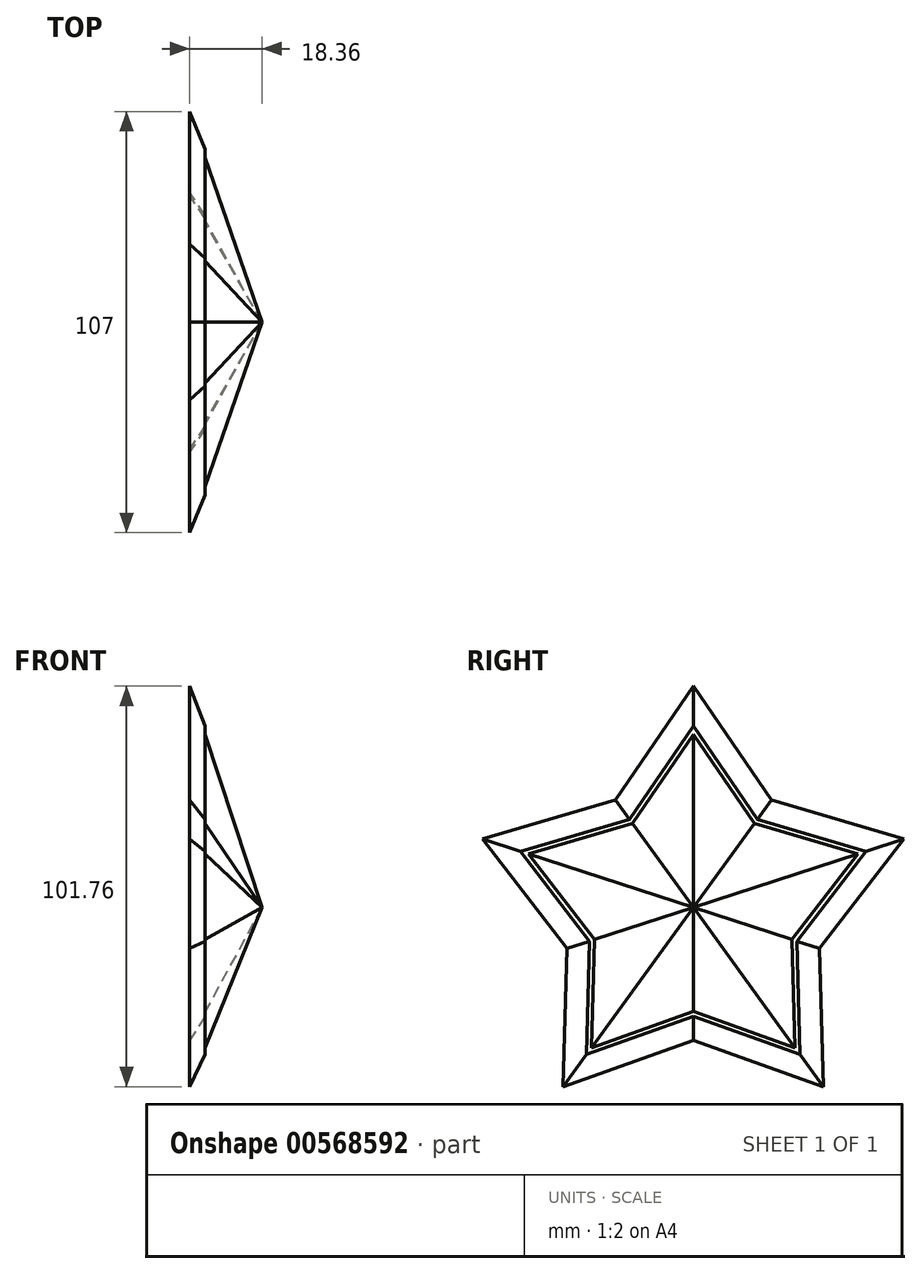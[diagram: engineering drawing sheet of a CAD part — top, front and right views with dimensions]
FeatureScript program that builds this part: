
annotation { "Feature Type Name" : "Feature", "Feature Type Description" : "" }
export const myFeature = defineFeature(function(context is Context, id is Id, definition is map)
    precondition{}
    {
        {
            var Q0;
            Q0=qCreatedBy(makeId("Right.planeOp"),FACE);
            var sketch = newSketch(context, id + "F0", { "sketchPlane" : qUnion([Q0])});
            skLineSegment(sketch, "E0", {"start": v(-53.5, 17.38) * mm, "end": v(-32.1, -10.43) * mm});
            skLineSegment(sketch, "E1", {"start": v(-32.1, -10.43) * mm, "end": v(-33.06, -45.5) * mm});
            skLineSegment(sketch, "E2", {"start": v(-33.06, -45.5) * mm, "end": v(0, -33.75) * mm});
            skLineSegment(sketch, "E3", {"start": v(0, -33.75) * mm, "end": v(33.06, -45.5) * mm});
            skLineSegment(sketch, "E4", {"start": v(33.06, -45.5) * mm, "end": v(32.1, -10.43) * mm});
            skLineSegment(sketch, "E5", {"start": v(32.1, -10.43) * mm, "end": v(53.5, 17.38) * mm});
            skLineSegment(sketch, "E6", {"start": v(53.5, 17.38) * mm, "end": v(19.84, 27.3) * mm});
            skLineSegment(sketch, "E7", {"start": v(19.84, 27.3) * mm, "end": v(0, 56.25) * mm});
            skLineSegment(sketch, "E8", {"start": v(0, 56.25) * mm, "end": v(-19.84, 27.3) * mm});
            skLineSegment(sketch, "E9", {"start": v(-19.84, 27.3) * mm, "end": v(-53.5, 17.38) * mm});
            skLineSegment(sketch, "E10", {"start": v(-33.06, -45.5) * mm, "end": v(0, 0) * mm});
            skLineSegment(sketch, "E11", {"start": v(0, 0) * mm, "end": v(33.06, -45.5) * mm});
            skLineSegment(sketch, "E12", {"start": v(0, 0) * mm, "end": v(53.5, 17.38) * mm});
            skLineSegment(sketch, "E13", {"start": v(0, 0) * mm, "end": v(0, 56.25) * mm});
            skLineSegment(sketch, "E14", {"start": v(0, 0) * mm, "end": v(-53.5, 17.38) * mm});
            skLineSegment(sketch, "E15", {"start": v(0, 0) * mm, "end": v(32.1, -10.43) * mm});
            skLineSegment(sketch, "E16", {"start": v(0, 0) * mm, "end": v(19.84, 27.3) * mm});
            skLineSegment(sketch, "E17", {"start": v(0, 0) * mm, "end": v(-19.84, 27.3) * mm});
            skLineSegment(sketch, "E18", {"start": v(0, 0) * mm, "end": v(-32.1, -10.43) * mm});
            skLineSegment(sketch, "E19", {"start": v(0, 0) * mm, "end": v(0, -33.75) * mm});
            skSolve(sketch);
        }
        {
            var Q0;
            Q0 = qSketchRegion(id + "F0", true);
            extrude(context, id + "F1", {"entities" : qUnion([Q0]), "depth" : 25 * mm, "offsetDistance" : 25 * mm, "hasDraft" : true, "draftAngle" : 60 * degree, "draftPullDirection" : true, "hasSecondDirection" : true, "secondDirectionOppositeDirection" : false, "secondDirectionDepth" : 4 * mm});
        }
        {
            var Q0;
            Q0 = qSketchRegion(id + "F0", true);
            extrude(context, id + "F2", {"entities" : qUnion([Q0]), "depth" : 4 * mm, "offsetDistance" : 25 * mm, "hasDraft" : true, "draftAngle" : 55 * degree, "draftPullDirection" : true});
        }
    });
